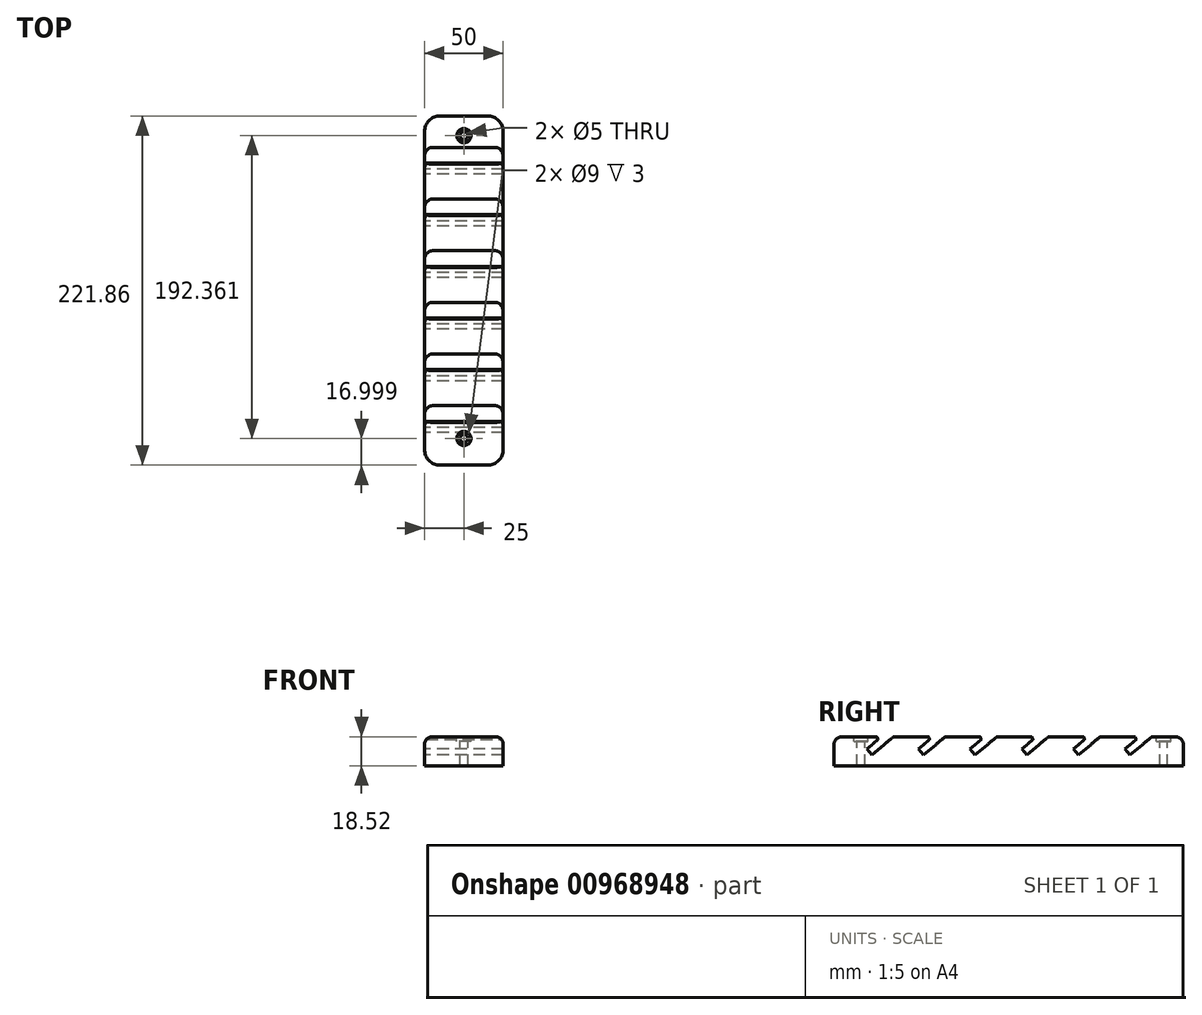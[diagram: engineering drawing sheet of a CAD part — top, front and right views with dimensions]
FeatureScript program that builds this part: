
annotation { "Feature Type Name" : "Feature", "Feature Type Description" : "" }
export const myFeature = defineFeature(function(context is Context, id is Id, definition is map)
    precondition{}
    {
        {
            var Q0;
            Q0=qCreatedBy(makeId("Right.planeOp"),FACE);
            var sketch = newSketch(context, id + "F0", { "sketchPlane" : qUnion([Q0])});
            skLineSegment(sketch, "E0", {"start": v(-105.93, -9.26) * mm, "end": v(105.93, -9.26) * mm});
            skLineSegment(sketch, "E1", {"start": v(105.93, -9.26) * mm, "end": v(105.93, 9.26) * mm});
            skLineSegment(sketch, "E2", {"start": v(105.93, 9.26) * mm, "end": v(85.93, 9.26) * mm});
            skLineSegment(sketch, "E3", {"start": v(85.93, 9.26) * mm, "end": v(72.1, -2.26) * mm});
            skLineSegment(sketch, "E4", {"start": v(68.9, 1.58) * mm, "end": v(78.12, 9.26) * mm});
            skLineSegment(sketch, "E5", {"start": v(78.12, 9.26) * mm, "end": v(53.12, 9.26) * mm});
            skLineSegment(sketch, "E6", {"start": v(53.12, 9.26) * mm, "end": v(39.3, -2.26) * mm});
            skLineSegment(sketch, "E7", {"start": v(36.1, 1.58) * mm, "end": v(45.31, 9.26) * mm});
            skLineSegment(sketch, "E8", {"start": v(45.31, 9.26) * mm, "end": v(20.31, 9.26) * mm});
            skLineSegment(sketch, "E9", {"start": v(20.31, 9.26) * mm, "end": v(6.48, -2.26) * mm});
            skLineSegment(sketch, "E10", {"start": v(3.28, 1.58) * mm, "end": v(12.5, 9.26) * mm});
            skLineSegment(sketch, "E11", {"start": v(12.5, 9.26) * mm, "end": v(-12.5, 9.26) * mm});
            skLineSegment(sketch, "E12", {"start": v(-12.5, 9.26) * mm, "end": v(-26.33, -2.26) * mm});
            skLineSegment(sketch, "E13", {"start": v(-29.53, 1.58) * mm, "end": v(-20.31, 9.26) * mm});
            skLineSegment(sketch, "E14", {"start": v(-20.31, 9.26) * mm, "end": v(-45.31, 9.26) * mm});
            skLineSegment(sketch, "E15", {"start": v(-45.31, 9.26) * mm, "end": v(-59.14, -2.26) * mm});
            skLineSegment(sketch, "E16", {"start": v(-62.34, 1.58) * mm, "end": v(-53.12, 9.26) * mm});
            skLineSegment(sketch, "E17", {"start": v(-53.12, 9.26) * mm, "end": v(-78.12, 9.26) * mm});
            skLineSegment(sketch, "E18", {"start": v(-78.12, 9.26) * mm, "end": v(-91.95, -2.26) * mm});
            skLineSegment(sketch, "E19", {"start": v(-95.15, 1.58) * mm, "end": v(-85.93, 9.26) * mm});
            skLineSegment(sketch, "E20", {"start": v(-85.93, 9.26) * mm, "end": v(-105.93, 9.26) * mm});
            skLineSegment(sketch, "E21", {"start": v(72.1, -2.26) * mm, "end": v(68.9, 1.58) * mm});
            skLineSegment(sketch, "E22", {"start": v(39.3, -2.26) * mm, "end": v(36.1, 1.58) * mm});
            skLineSegment(sketch, "E23", {"start": v(6.48, -2.26) * mm, "end": v(3.28, 1.58) * mm});
            skLineSegment(sketch, "E24", {"start": v(-26.33, -2.26) * mm, "end": v(-29.53, 1.58) * mm});
            skLineSegment(sketch, "E25", {"start": v(-59.14, -2.26) * mm, "end": v(-62.34, 1.58) * mm});
            skLineSegment(sketch, "E26", {"start": v(-91.95, -2.26) * mm, "end": v(-95.15, 1.58) * mm});
            skLineSegment(sketch, "E27.bottom", {"start": v(-105.93, 9.26) * mm, "end": v(-115.93, 9.26) * mm});
            skLineSegment(sketch, "E27.top", {"start": v(-105.93, -9.26) * mm, "end": v(-115.93, -9.26) * mm});
            skLineSegment(sketch, "E27.right", {"start": v(-115.93, 9.26) * mm, "end": v(-115.93, -9.26) * mm});
            skSolve(sketch);
        }
        {
            var Q0;
            Q0=makeQuery(id+"F0.imprint","IMPRINT",FACE,{"disambiguationData":[TD([[makeQuery(id+"F0.imprint","IMPRINT",EDGE,{"derivedFrom":sQuery(id+"F0.wireOp",EDGE,"E0")}),1.0]])]});
            extrude(context, id + "F1", {"entities" : qUnion([Q0]), "endBound" : BoundingType.SYMMETRIC, "depth" : 50 * mm, "offsetDistance" : 25 * mm});
        }
        {
            var Q0;
            Q0=makeQuery(id+"F1.opExtrude","SWEPT_EDGE",EDGE,{"disambiguationData":[OSD([sQuery(id+"F0.wireOp",EDGE,"E19"),sQuery(id+"F0.wireOp",EDGE,"E20")])]});
            var Q1;
            Q1=makeQuery(id+"F1.opExtrude","SWEPT_EDGE",EDGE,{"disambiguationData":[OSD([sQuery(id+"F0.wireOp",EDGE,"E16"),sQuery(id+"F0.wireOp",EDGE,"E17")])]});
            var Q2;
            Q2=makeQuery(id+"F1.opExtrude","SWEPT_EDGE",EDGE,{"disambiguationData":[OSD([sQuery(id+"F0.wireOp",EDGE,"E13"),sQuery(id+"F0.wireOp",EDGE,"E14")])]});
            var Q3;
            Q3=makeQuery(id+"F1.opExtrude","SWEPT_EDGE",EDGE,{"disambiguationData":[OSD([sQuery(id+"F0.wireOp",EDGE,"E10"),sQuery(id+"F0.wireOp",EDGE,"E11")])]});
            var Q4;
            Q4=makeQuery(id+"F1.opExtrude","SWEPT_EDGE",EDGE,{"disambiguationData":[OSD([sQuery(id+"F0.wireOp",EDGE,"E7"),sQuery(id+"F0.wireOp",EDGE,"E8")])]});
            var Q5;
            Q5=makeQuery(id+"F1.opExtrude","SWEPT_EDGE",EDGE,{"disambiguationData":[OSD([sQuery(id+"F0.wireOp",EDGE,"E4"),sQuery(id+"F0.wireOp",EDGE,"E5")])]});
            chamfer(context, id + "F2", {"entities" : qUnion([Q0, Q1, Q2, Q3, Q4, Q5]), "width" : 1 * mm, "tangentPropagation" : true});
        }
        {
            var Q0;
            Q0=makeQuery(id+"F1.opExtrude","CAP_EDGE",EDGE,{"disambiguationData":[OSD([sQuery(id+"F0.wireOp",EDGE,"E27.right")])],"isStart":false});
            var Q1;
            Q1=makeQuery(id+"F1.opExtrude","CAP_EDGE",EDGE,{"disambiguationData":[OSD([sQuery(id+"F0.wireOp",EDGE,"E27.right")])],"isStart":true});
            var Q2;
            Q2=makeQuery(id+"F1.opExtrude","CAP_EDGE",EDGE,{"disambiguationData":[OSD([sQuery(id+"F0.wireOp",EDGE,"E1")])],"isStart":false});
            var Q3;
            Q3=makeQuery(id+"F1.opExtrude","CAP_EDGE",EDGE,{"disambiguationData":[OSD([sQuery(id+"F0.wireOp",EDGE,"E1")])],"isStart":true});
            fillet(context, id + "F3", {"entities" : qUnion([Q0, Q1, Q2, Q3]), "radius" : 10 * mm, "tangentPropagation" : true, "allowEdgeOverflow" : false});
        }
        {
            var Q0;
            Q0=makeQuery(id+"F1.opExtrude","SWEPT_EDGE",EDGE,{"disambiguationData":[OSD([sQuery(id+"F0.wireOp",EDGE,"E1"),sQuery(id+"F0.wireOp",EDGE,"E2")])]});
            var Q1;
            Q1=makeQuery(id+"F3.opFillet","BLEND_EDGE",EDGE,{"blendedFrom":[makeQuery(id+"F1.opExtrude","CAP_EDGE",EDGE,{"disambiguationData":[OSD([sQuery(id+"F0.wireOp",EDGE,"E1")])],"isStart":false}),makeQuery(id+"F1.opExtrude","SWEPT_FACE",FACE,{"disambiguationData":[OSD([sQuery(id+"F0.wireOp",EDGE,"E2")])]})],"blendedInto":[makeQuery(id+"F1.opExtrude","SWEPT_FACE",FACE,{"disambiguationData":[OSD([sQuery(id+"F0.wireOp",EDGE,"E2")])]})]});
            var Q2;
            Q2=makeQuery(id+"F1.opExtrude","CAP_EDGE",EDGE,{"disambiguationData":[OSD([sQuery(id+"F0.wireOp",EDGE,"E2")])],"isStart":false});
            var Q3;
            Q3=makeQuery(id+"F1.opExtrude","CAP_EDGE",EDGE,{"disambiguationData":[OSD([sQuery(id+"F0.wireOp",EDGE,"E5")])],"isStart":false});
            var Q4;
            Q4=makeQuery(id+"F1.opExtrude","CAP_EDGE",EDGE,{"disambiguationData":[OSD([sQuery(id+"F0.wireOp",EDGE,"E8")])],"isStart":false});
            var Q5;
            Q5=makeQuery(id+"F1.opExtrude","CAP_EDGE",EDGE,{"disambiguationData":[OSD([sQuery(id+"F0.wireOp",EDGE,"E11")])],"isStart":false});
            var Q6;
            Q6=makeQuery(id+"F1.opExtrude","CAP_EDGE",EDGE,{"disambiguationData":[OSD([sQuery(id+"F0.wireOp",EDGE,"E14")])],"isStart":false});
            var Q7;
            Q7=makeQuery(id+"F1.opExtrude","CAP_EDGE",EDGE,{"disambiguationData":[OSD([sQuery(id+"F0.wireOp",EDGE,"E17")])],"isStart":false});
            var Q8;
            Q8=makeQuery(id+"F1.opExtrude","CAP_EDGE",EDGE,{"disambiguationData":[OSD([sQuery(id+"F0.wireOp",EDGE,"E20"),sQuery(id+"F0.wireOp",EDGE,"E27.bottom")])],"isStart":false});
            var Q9;
            Q9=makeQuery(id+"F3.opFillet","BLEND_EDGE",EDGE,{"blendedFrom":[makeQuery(id+"F1.opExtrude","CAP_EDGE",EDGE,{"disambiguationData":[OSD([sQuery(id+"F0.wireOp",EDGE,"E27.right")])],"isStart":false}),makeQuery(id+"F1.opExtrude","SWEPT_FACE",FACE,{"disambiguationData":[OSD([sQuery(id+"F0.wireOp",EDGE,"E20"),sQuery(id+"F0.wireOp",EDGE,"E27.bottom")])]})],"blendedInto":[makeQuery(id+"F1.opExtrude","SWEPT_FACE",FACE,{"disambiguationData":[OSD([sQuery(id+"F0.wireOp",EDGE,"E20"),sQuery(id+"F0.wireOp",EDGE,"E27.bottom")])]})]});
            var Q10;
            Q10=makeQuery(id+"F1.opExtrude","SWEPT_EDGE",EDGE,{"disambiguationData":[OSD([sQuery(id+"F0.wireOp",EDGE,"E27.bottom"),sQuery(id+"F0.wireOp",EDGE,"E27.right")])]});
            var Q11;
            Q11=makeQuery(id+"F3.opFillet","BLEND_EDGE",EDGE,{"blendedFrom":[makeQuery(id+"F1.opExtrude","CAP_EDGE",EDGE,{"disambiguationData":[OSD([sQuery(id+"F0.wireOp",EDGE,"E27.right")])],"isStart":true}),makeQuery(id+"F1.opExtrude","SWEPT_FACE",FACE,{"disambiguationData":[OSD([sQuery(id+"F0.wireOp",EDGE,"E20"),sQuery(id+"F0.wireOp",EDGE,"E27.bottom")])]})],"blendedInto":[makeQuery(id+"F1.opExtrude","SWEPT_FACE",FACE,{"disambiguationData":[OSD([sQuery(id+"F0.wireOp",EDGE,"E20"),sQuery(id+"F0.wireOp",EDGE,"E27.bottom")])]})]});
            var Q12;
            Q12=makeQuery(id+"F1.opExtrude","CAP_EDGE",EDGE,{"disambiguationData":[OSD([sQuery(id+"F0.wireOp",EDGE,"E20"),sQuery(id+"F0.wireOp",EDGE,"E27.bottom")])],"isStart":true});
            var Q13;
            Q13=makeQuery(id+"F1.opExtrude","CAP_EDGE",EDGE,{"disambiguationData":[OSD([sQuery(id+"F0.wireOp",EDGE,"E17")])],"isStart":true});
            var Q14;
            Q14=makeQuery(id+"F1.opExtrude","CAP_EDGE",EDGE,{"disambiguationData":[OSD([sQuery(id+"F0.wireOp",EDGE,"E14")])],"isStart":true});
            var Q15;
            Q15=makeQuery(id+"F1.opExtrude","CAP_EDGE",EDGE,{"disambiguationData":[OSD([sQuery(id+"F0.wireOp",EDGE,"E11")])],"isStart":true});
            var Q16;
            Q16=makeQuery(id+"F1.opExtrude","CAP_EDGE",EDGE,{"disambiguationData":[OSD([sQuery(id+"F0.wireOp",EDGE,"E8")])],"isStart":true});
            var Q17;
            Q17=makeQuery(id+"F1.opExtrude","CAP_EDGE",EDGE,{"disambiguationData":[OSD([sQuery(id+"F0.wireOp",EDGE,"E5")])],"isStart":true});
            var Q18;
            Q18=makeQuery(id+"F3.opFillet","BLEND_EDGE",EDGE,{"blendedFrom":[makeQuery(id+"F1.opExtrude","CAP_EDGE",EDGE,{"disambiguationData":[OSD([sQuery(id+"F0.wireOp",EDGE,"E1")])],"isStart":true}),makeQuery(id+"F1.opExtrude","SWEPT_FACE",FACE,{"disambiguationData":[OSD([sQuery(id+"F0.wireOp",EDGE,"E2")])]})],"blendedInto":[makeQuery(id+"F1.opExtrude","SWEPT_FACE",FACE,{"disambiguationData":[OSD([sQuery(id+"F0.wireOp",EDGE,"E2")])]})]});
            fillet(context, id + "F4", {"entities" : qUnion([Q0, Q1, Q2, Q3, Q4, Q5, Q6, Q7, Q8, Q9, Q10, Q11, Q12, Q13, Q14, Q15, Q16, Q17, Q18]), "radius" : 5 * mm, "tangentPropagation" : true, "allowEdgeOverflow" : false});
        }
        {
            var Q0;
            Q0=makeQuery(id+"F1.opExtrude","SWEPT_FACE",FACE,{"disambiguationData":[OSD([sQuery(id+"F0.wireOp",EDGE,"E20"),sQuery(id+"F0.wireOp",EDGE,"E27.bottom")])]});
            var sketch = newSketch(context, id + "F5", { "sketchPlane" : qUnion([Q0])});
            skLineSegment(sketch, "E28", {"start": v(0, -86.93) * mm, "end": v(0, -110.93) * mm, "construction": true});
            skCircle(sketch, "E29", {"center": v(0, -98.93) * mm, "radius": 2.5 * mm});
            skCircle(sketch, "E30", {"center": v(0, -98.93) * mm, "radius": 4.5 * mm});
            skSolve(sketch);
        }
        {
            var Q0;
            Q0=makeQuery(id+"F5.imprint","IMPRINT",FACE,{"disambiguationData":[TD([[makeQuery(id+"F5.imprint","IMPRINT",EDGE,{"derivedFrom":sQuery(id+"F5.wireOp",EDGE,"E29")}),1.0]])]});
            extrude(context, id + "F6", {"entities" : qUnion([Q0]), "operationType" : NewBodyOperationType.REMOVE, "oppositeDirection" : true, "depth" : 25 * mm, "offsetDistance" : 25 * mm});
        }
        {
            var Q0;
            Q0=makeQuery(id+"F5.imprint","IMPRINT",FACE,{"disambiguationData":[TD([[makeQuery(id+"F5.imprint","IMPRINT",EDGE,{"derivedFrom":sQuery(id+"F5.wireOp",EDGE,"E29")}),-1.0]])]});
            extrude(context, id + "F7", {"entities" : qUnion([Q0]), "operationType" : NewBodyOperationType.REMOVE, "oppositeDirection" : true, "depth" : 3 * mm, "offsetDistance" : 25 * mm});
        }
        {
            var Q0;
            Q0=makeQuery(id+"F1.opExtrude","SWEPT_FACE",FACE,{"disambiguationData":[OSD([sQuery(id+"F0.wireOp",EDGE,"E2")])]});
            var sketch = newSketch(context, id + "F8", { "sketchPlane" : qUnion([Q0])});
            skLineSegment(sketch, "E31", {"start": v(0, 100.93) * mm, "end": v(0, 85.93) * mm, "construction": true});
            skCircle(sketch, "E32", {"center": v(0, 93.43) * mm, "radius": 4.5 * mm});
            skCircle(sketch, "E33", {"center": v(0, 93.43) * mm, "radius": 2.5 * mm});
            skSolve(sketch);
        }
        {
            var Q0;
            Q0=makeQuery(id+"F8.imprint","IMPRINT",FACE,{"disambiguationData":[TD([[makeQuery(id+"F8.imprint","IMPRINT",EDGE,{"derivedFrom":sQuery(id+"F8.wireOp",EDGE,"E33")}),1.0]])]});
            extrude(context, id + "F9", {"entities" : qUnion([Q0]), "operationType" : NewBodyOperationType.REMOVE, "oppositeDirection" : true, "depth" : 25 * mm, "offsetDistance" : 25 * mm});
        }
        {
            var Q0;
            Q0=makeQuery(id+"F8.imprint","IMPRINT",FACE,{"disambiguationData":[TD([[makeQuery(id+"F8.imprint","IMPRINT",EDGE,{"derivedFrom":sQuery(id+"F8.wireOp",EDGE,"E32")}),1.0]])]});
            extrude(context, id + "F10", {"entities" : qUnion([Q0]), "operationType" : NewBodyOperationType.REMOVE, "oppositeDirection" : true, "depth" : 3 * mm, "offsetDistance" : 25 * mm});
        }
    });
